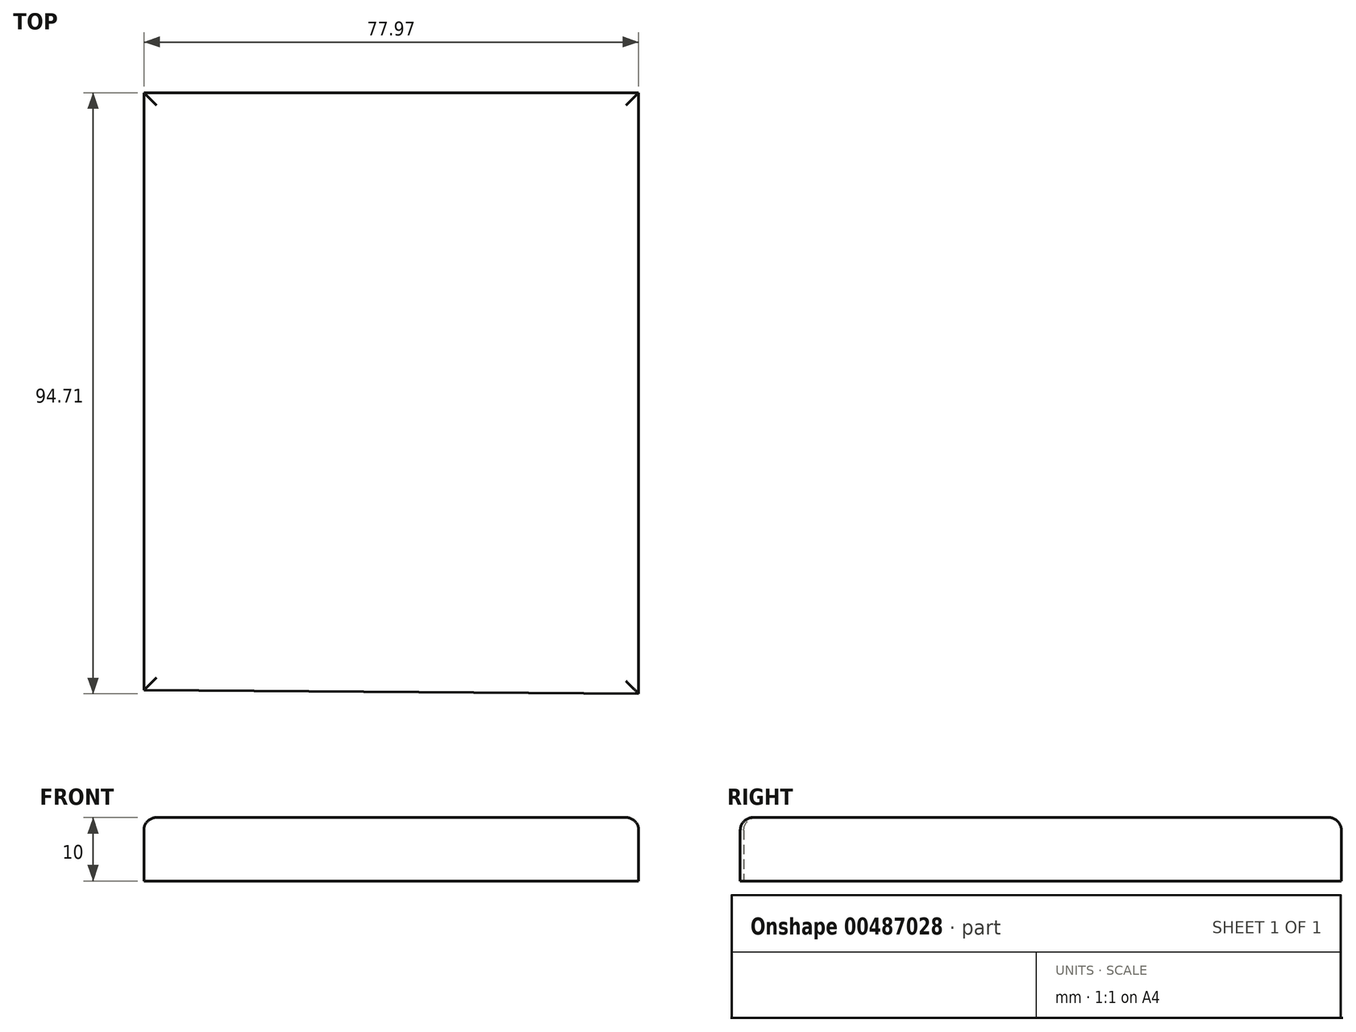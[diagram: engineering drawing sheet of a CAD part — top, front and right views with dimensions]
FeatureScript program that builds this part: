
annotation { "Feature Type Name" : "Feature", "Feature Type Description" : "" }
export const myFeature = defineFeature(function(context is Context, id is Id, definition is map)
    precondition{}
    {
        {
            var Q0;
            Q0=qCreatedBy(makeId("Top.planeOp"),FACE);
            var sketch = newSketch(context, id + "F0", { "sketchPlane" : qUnion([Q0])});
            skLineSegment(sketch, "E0", {"start": v(-33.59, -44.84) * mm, "end": v(-33.59, 49.3) * mm});
            skLineSegment(sketch, "E1", {"start": v(-33.59, 49.3) * mm, "end": v(44.38, 49.3) * mm});
            skLineSegment(sketch, "E2", {"start": v(44.38, 49.3) * mm, "end": v(44.38, -45.4) * mm});
            skLineSegment(sketch, "E3", {"start": v(44.38, -45.4) * mm, "end": v(-33.59, -44.84) * mm});
            skSolve(sketch);
        }
        {
            var Q0;
            Q0=makeQuery(id+"F0.imprint","IMPRINT",FACE,{"disambiguationData":[TD([[makeQuery(id+"F0.imprint","IMPRINT",EDGE,{"derivedFrom":sQuery(id+"F0.wireOp",EDGE,"E0")}),-1.0]])]});
            extrude(context, id + "F1", {"entities" : qUnion([Q0]), "depth" : 10 * mm});
        }
        {
            var Q0;
            Q0=makeQuery(id+"F1.opExtrude","CAP_FACE",FACE,{"disambiguationData":[OSD([sQuery(id+"F0.wireOp",EDGE,"E0"),sQuery(id+"F0.wireOp",EDGE,"E1"),sQuery(id+"F0.wireOp",EDGE,"E2"),sQuery(id+"F0.wireOp",EDGE,"E3")])],"isStart":false});
            fillet(context, id + "F2", {"entities" : qUnion([Q0]), "radius" : 2 * mm, "tangentPropagation" : true, "allowEdgeOverflow" : false});
        }
    });
